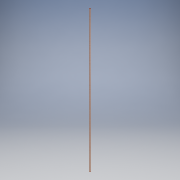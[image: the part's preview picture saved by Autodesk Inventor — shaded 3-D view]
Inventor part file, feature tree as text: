
AUTODESK INVENTOR PART (.ipt)
format: ipt  version: 2018 (Build 220112000, 112)  size: 91,648 bytes
history: native  units: mm
features: other x1, extrude x1, sketch x1
ambient origin geometry x8: Origin, YZ Plane, XZ Plane, XY Plane, X Axis, Y Axis, Z Axis, Center Point
bodies: Body1 (feature_tree)
feature tree (3):
  other  "ソリッド1"
  extrude  "押し出し1"  Depth=6.0mm
  sketch  "スケッチ1"
